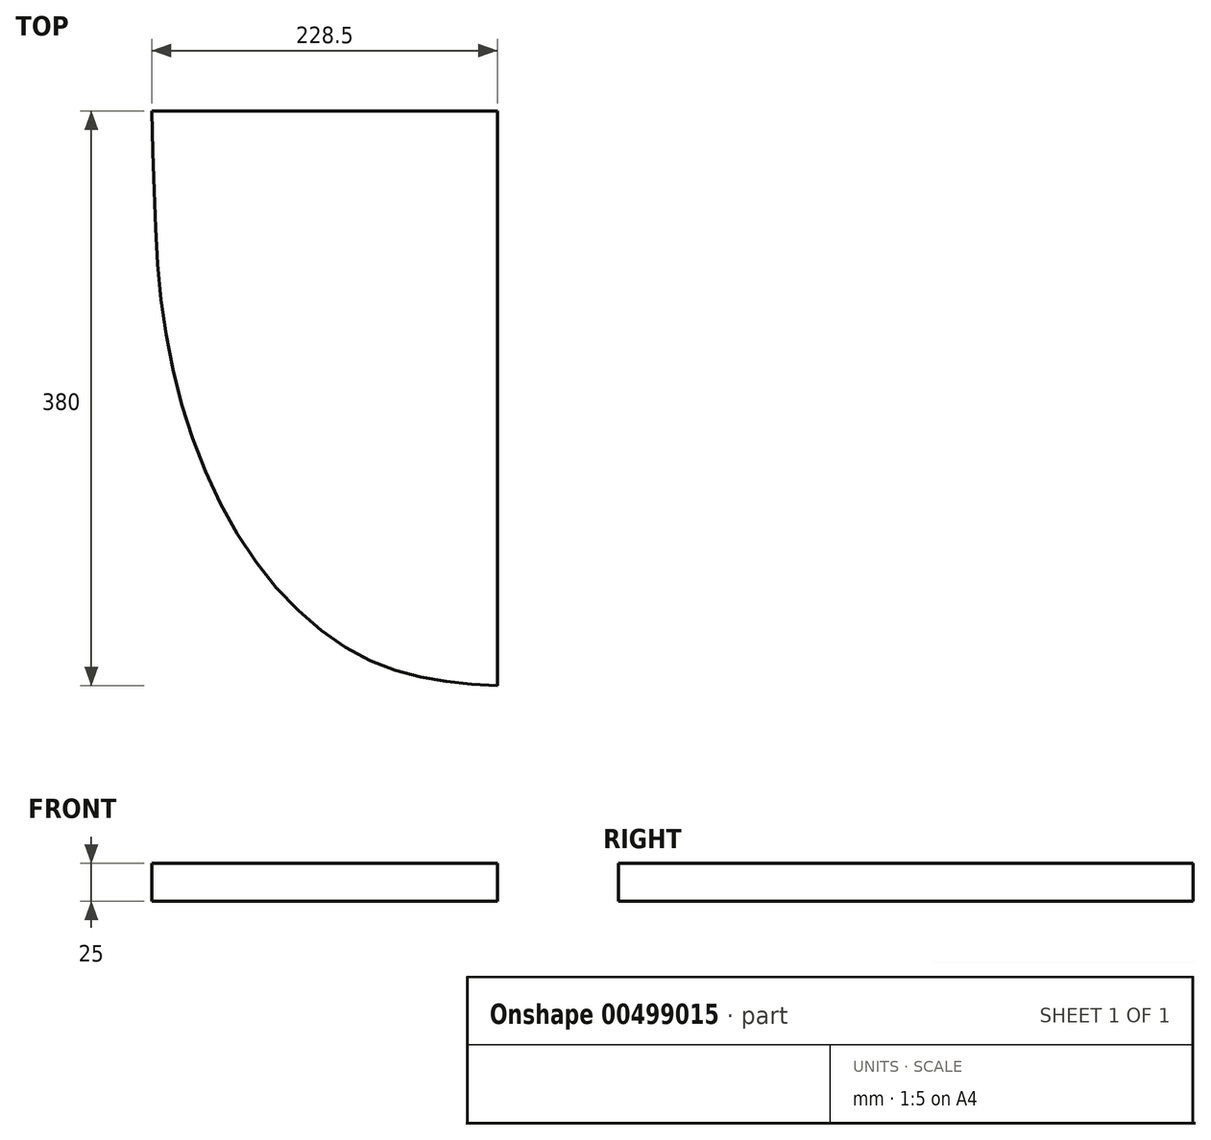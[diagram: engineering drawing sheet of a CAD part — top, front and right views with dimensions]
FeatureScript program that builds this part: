
annotation { "Feature Type Name" : "Feature", "Feature Type Description" : "" }
export const myFeature = defineFeature(function(context is Context, id is Id, definition is map)
    precondition{}
    {
        {
            var Q0;
            Q0=qCreatedBy(makeId("Top.planeOp"),FACE);
            var sketch = newSketch(context, id + "F0", { "sketchPlane" : qUnion([Q0])});
            skPoint(sketch, "E0.first.point", {"position": v(-228.5, 0) * mm});
            skLineSegment(sketch, "E1", {"start": v(0, 0) * mm, "end": v(0, 72.32) * mm});
            skFitSpline(sketch, "E2.MirrorCS", {"points": [v(-228.5, 0) * mm, v(-216.24, -163.43) * mm, v(-160.12, -297.54) * mm, v(-78.33, -366.02) * mm, v(0, -380) * mm], "startDerivative": vector(17.55, -632.9) * mm, "endDerivative": vector(389.13, -21.18) * mm});
            skLineSegment(sketch, "E3", {"start": v(-228.5, 0) * mm, "end": v(0, 0) * mm});
            skLineSegment(sketch, "E4", {"start": v(0, 0) * mm, "end": v(0, -380) * mm});
            skSolve(sketch);
        }
        {
            var Q0;
            Q0=makeQuery(id+"F0.imprint","IMPRINT",FACE,{"disambiguationData":[TD([[makeQuery(id+"F0.imprint","IMPRINT",EDGE,{"derivedFrom":sQuery(id+"F0.wireOp",EDGE,"f762cab6-bf76-4882-9f69-acd85c3c14cd")}),-1.0]])]});
            var Q1;
            {var subQ0=sQuery(id+"F0.wireOp",EDGE,"E2.MirrorCS");Q1=makeQuery(id+"F0.imprint","IMPRINT",FACE,{"disambiguationData":[TD([[makeQuery(id+"F0.imprint","IMPRINT",EDGE,{"derivedFrom":subQ0}),1.0]])]});}
            extrude(context, id + "F1", {"entities" : qUnion([Q0, Q1]), "depth" : 25 * mm});
        }
    });
